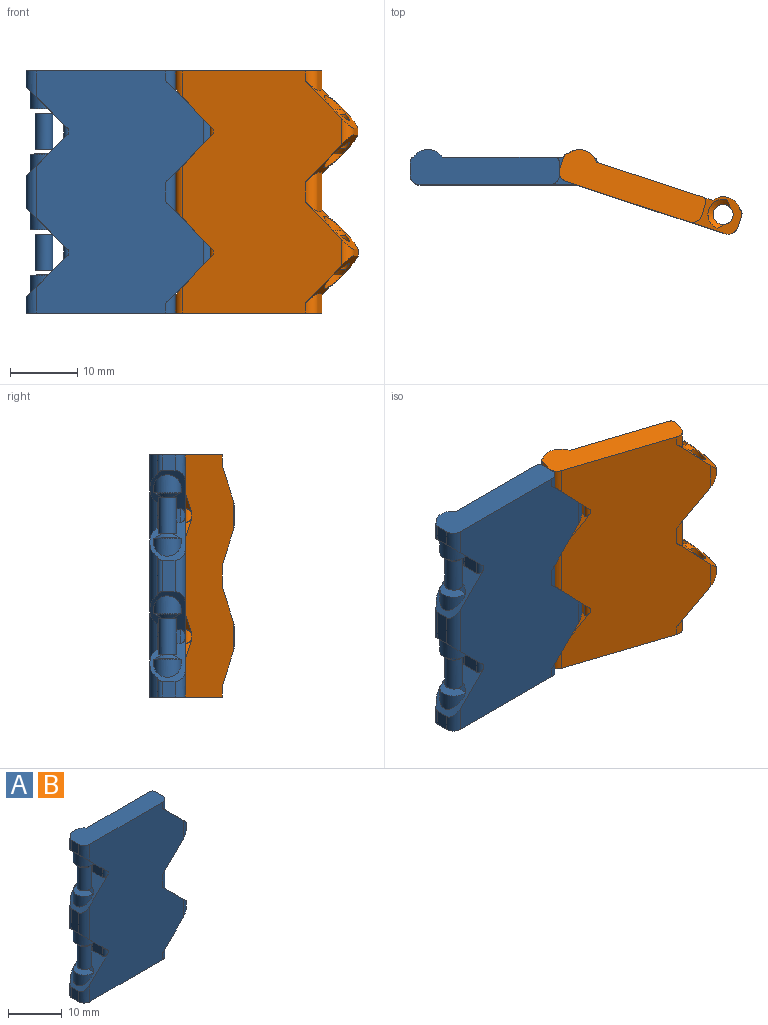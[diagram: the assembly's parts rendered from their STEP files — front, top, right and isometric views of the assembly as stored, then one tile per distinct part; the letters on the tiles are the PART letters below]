
ASSEMBLY  parts=2 mates=1
PART A: 67 faces, bbox 28x5.4x36.2 mm
  f0: plane 36x24.83mm, normal (0,-1,0), area 746.1mm2, adj f5,f11,f12,f13,f21,f23,f24,f26
  f1: cylinder r=2.62mm len=10.59mm, axis (0,0,1), area 31.7mm2, adj f2,f5,f9,f26
  f2: plane 36x18.19mm, normal (0,1,0), area 630.1mm2, adj f1,f5,f10,f13,f14,f20,f24,f26
  f3: plane 1.92x0.95mm, normal (1,0,0), area 1.8mm2, adj f5,f9,f11,f26
  f4: plane 5.8x1.88mm, normal (1,0,0), area 10.9mm2, adj f5,f10,f12,f40
  f5: plane 7.29x7.29mm, normal (0.71,0,0.71), area 20.9mm2, adj f0,f1,f2,f3,f4,f6,f7,f8
  f6: cylinder r=2.25mm len=4.49mm, axis (0,0,-1), area 9mm2, adj f5,f7
  f7: cone r=2.2mm half-angle=45deg, axis (0,0,1), area 6.8mm2, adj f5,f6,f8
  f8: cylinder r=1.5mm len=5.09mm, axis (0,0,-1), area 43.9mm2, adj f5,f7,f26,f28
  f9: cylinder r=0.75mm len=1.97mm, axis (0,0,1), area 1.2mm2, adj f1,f3,f5,f26
  f10: cylinder r=0.75mm len=5.8mm, axis (0,0,-1), area 6.2mm2, adj f2,f4,f5,f40
  f11: cylinder r=1.5mm len=3.95mm, axis (0,0,1), area 4.8mm2, adj f0,f3,f5,f26
  f12: cylinder r=1.5mm len=5.8mm, axis (0,0,1), area 11.1mm2, adj f0,f4,f5,f40
  f13: plane 6.38x6.38mm, normal (-0.71,0,-0.71), area 21.5mm2, adj f0,f2,f14,f15,f16,f17,f18,f20
  f14: cylinder r=2.62mm len=14.34mm, axis (0,0,1), area 50.7mm2, adj f2,f13,f22,f46
  f15: plane 4.7x1.92mm, normal (-1,0,0), area 9mm2, adj f13,f22,f23,f46
  f16: plane 2.63x2.05mm, normal (-1,0,0), area 5.4mm2, adj f13,f20,f21,f31
  f17: cylinder r=2.06mm len=4.13mm, axis (0,0,-1), area 12.8mm2, adj f13,f18
  f18: cone r=2.06mm half-angle=45deg, axis (0,0,1), area 8mm2, adj f13,f17,f19
  f19: cylinder r=1.31mm len=5.25mm, axis (0,0,-1), area 43.3mm2, adj f18,f35
  f20: cylinder r=0.75mm len=2.05mm, axis (0,0,1), area 1.8mm2, adj f2,f13,f16,f31
  f21: cylinder r=0.75mm len=2.05mm, axis (0,0,-1), area 1.8mm2, adj f0,f13,f16,f31
  f22: cylinder r=0.75mm len=5.72mm, axis (0,0,1), area 4.7mm2, adj f13,f14,f15,f46
  f23: cylinder r=1.5mm len=7.7mm, axis (0,0,-1), area 13.6mm2, adj f0,f13,f15,f46
  f24: plane 22.2x5.25mm, normal (0,0,-1), area 93.8mm2, adj f0,f2,f25,f29,f30,f32,f33,f36
  f25: plane 2.9x1.88mm, normal (1,0,0), area 5.4mm2, adj f24,f26,f29,f30
  f26: plane 7.29x7.29mm, normal (0.71,0,-0.71), area 20.9mm2, adj f0,f1,f2,f3,f8,f9,f11,f25
  f27: cylinder r=2.25mm len=4.49mm, axis (0,0,1), area 9mm2, adj f26,f28
  f28: cone r=2.2mm half-angle=45deg, axis (0,0,-1), area 6.8mm2, adj f8,f26,f27
  f29: cylinder r=0.75mm len=2.9mm, axis (0,0,1), area 3.1mm2, adj f2,f24,f25,f26
  f30: cylinder r=1.5mm len=2.9mm, axis (0,0,-1), area 5.5mm2, adj f0,f24,f25,f26
  f31: plane 6.38x6.38mm, normal (-0.71,0,0.71), area 21.5mm2, adj f0,f2,f16,f20,f21,f32,f33,f34
  f32: cylinder r=2.62mm len=7.17mm, axis (0,0,-1), area 25.3mm2, adj f2,f24,f31,f36
  f33: plane 2.35x1.92mm, normal (-1,0,0), area 4.5mm2, adj f24,f31,f36,f37
  f34: cylinder r=2.06mm len=4.13mm, axis (0,0,1), area 12.8mm2, adj f31,f35
  f35: cone r=2.06mm half-angle=45deg, axis (0,0,-1), area 8mm2, adj f19,f31,f34
  f36: cylinder r=0.75mm len=2.86mm, axis (0,0,-1), area 2.4mm2, adj f24,f31,f32,f33
  f37: cylinder r=1.5mm len=3.85mm, axis (0,0,1), area 6.8mm2, adj f0,f24,f31,f33
  f38: cylinder r=2.62mm len=10.59mm, axis (0,0,-1), area 31.7mm2, adj f2,f40,f44,f55
  f39: plane 1.92x0.95mm, normal (1,0,0), area 1.8mm2, adj f40,f44,f45,f55
  f40: plane 7.29x7.29mm, normal (0.71,0,-0.71), area 20.9mm2, adj f0,f2,f4,f10,f12,f38,f39,f41
  f41: cylinder r=2.25mm len=4.49mm, axis (0,0,1), area 9mm2, adj f40,f42
  f42: cone r=2.2mm half-angle=45deg, axis (0,0,-1), area 6.8mm2, adj f40,f41,f43
  f43: cylinder r=1.5mm len=5.09mm, axis (0,0,1), area 43.9mm2, adj f40,f42,f55,f57
  f44: cylinder r=0.75mm len=1.97mm, axis (0,0,-1), area 1.2mm2, adj f38,f39,f40,f55
  f45: cylinder r=1.5mm len=3.95mm, axis (0,0,-1), area 4.8mm2, adj f0,f39,f40,f55
  f46: plane 6.38x6.38mm, normal (-0.71,0,0.71), area 21.5mm2, adj f0,f2,f14,f15,f22,f23,f47,f48
  f47: plane 2.63x2.05mm, normal (-1,0,0), area 5.4mm2, adj f46,f51,f52,f60
  f48: cylinder r=2.06mm len=4.13mm, axis (0,0,1), area 12.8mm2, adj f46,f49
  f49: cone r=2.06mm half-angle=45deg, axis (0,0,-1), area 8mm2, adj f46,f48,f50
  f50: cylinder r=1.31mm len=5.25mm, axis (0,0,1), area 43.3mm2, adj f49,f64
  f51: cylinder r=0.75mm len=2.05mm, axis (0,0,-1), area 1.8mm2, adj f2,f46,f47,f60
  f52: cylinder r=0.75mm len=2.05mm, axis (0,0,1), area 1.8mm2, adj f0,f46,f47,f60
  f53: plane 22.2x5.25mm, normal (0,0,1), area 93.8mm2, adj f0,f2,f54,f58,f59,f61,f62,f65
  f54: plane 2.9x1.88mm, normal (1,0,0), area 5.4mm2, adj f53,f55,f58,f59
  f55: plane 7.29x7.29mm, normal (0.71,0,0.71), area 20.9mm2, adj f0,f2,f38,f39,f43,f44,f45,f54
  f56: cylinder r=2.25mm len=4.49mm, axis (0,0,-1), area 9mm2, adj f55,f57
  f57: cone r=2.2mm half-angle=45deg, axis (0,0,1), area 6.8mm2, adj f43,f55,f56
  f58: cylinder r=0.75mm len=2.9mm, axis (0,0,-1), area 3.1mm2, adj f2,f53,f54,f55
  f59: cylinder r=1.5mm len=2.9mm, axis (0,0,1), area 5.5mm2, adj f0,f53,f54,f55
  f60: plane 6.38x6.38mm, normal (-0.71,0,-0.71), area 21.5mm2, adj f0,f2,f47,f51,f52,f61,f62,f63
  f61: cylinder r=2.62mm len=7.17mm, axis (0,0,1), area 25.3mm2, adj f2,f53,f60,f65
  f62: plane 2.35x1.92mm, normal (-1,0,0), area 4.5mm2, adj f53,f60,f65,f66
  f63: cylinder r=2.06mm len=4.13mm, axis (0,0,-1), area 12.8mm2, adj f60,f64
  f64: cone r=2.06mm half-angle=45deg, axis (0,0,1), area 8mm2, adj f50,f60,f63
  f65: cylinder r=0.75mm len=2.86mm, axis (0,0,1), area 2.4mm2, adj f53,f60,f61,f62
  f66: cylinder r=1.5mm len=3.85mm, axis (0,0,-1), area 6.8mm2, adj f0,f53,f60,f62
PART B: same geometry as A
PLACE A t=(5.05,-7.83,0.61)mm fixed
PLACE B rot(axis=(0,0,-1),18.1deg) t=(26.44,-14.83,0.61)mm
MATE revolute A.f1 <-> B.f14  axis (0,0,1) through (5.05,-7.83,18.61)mm
